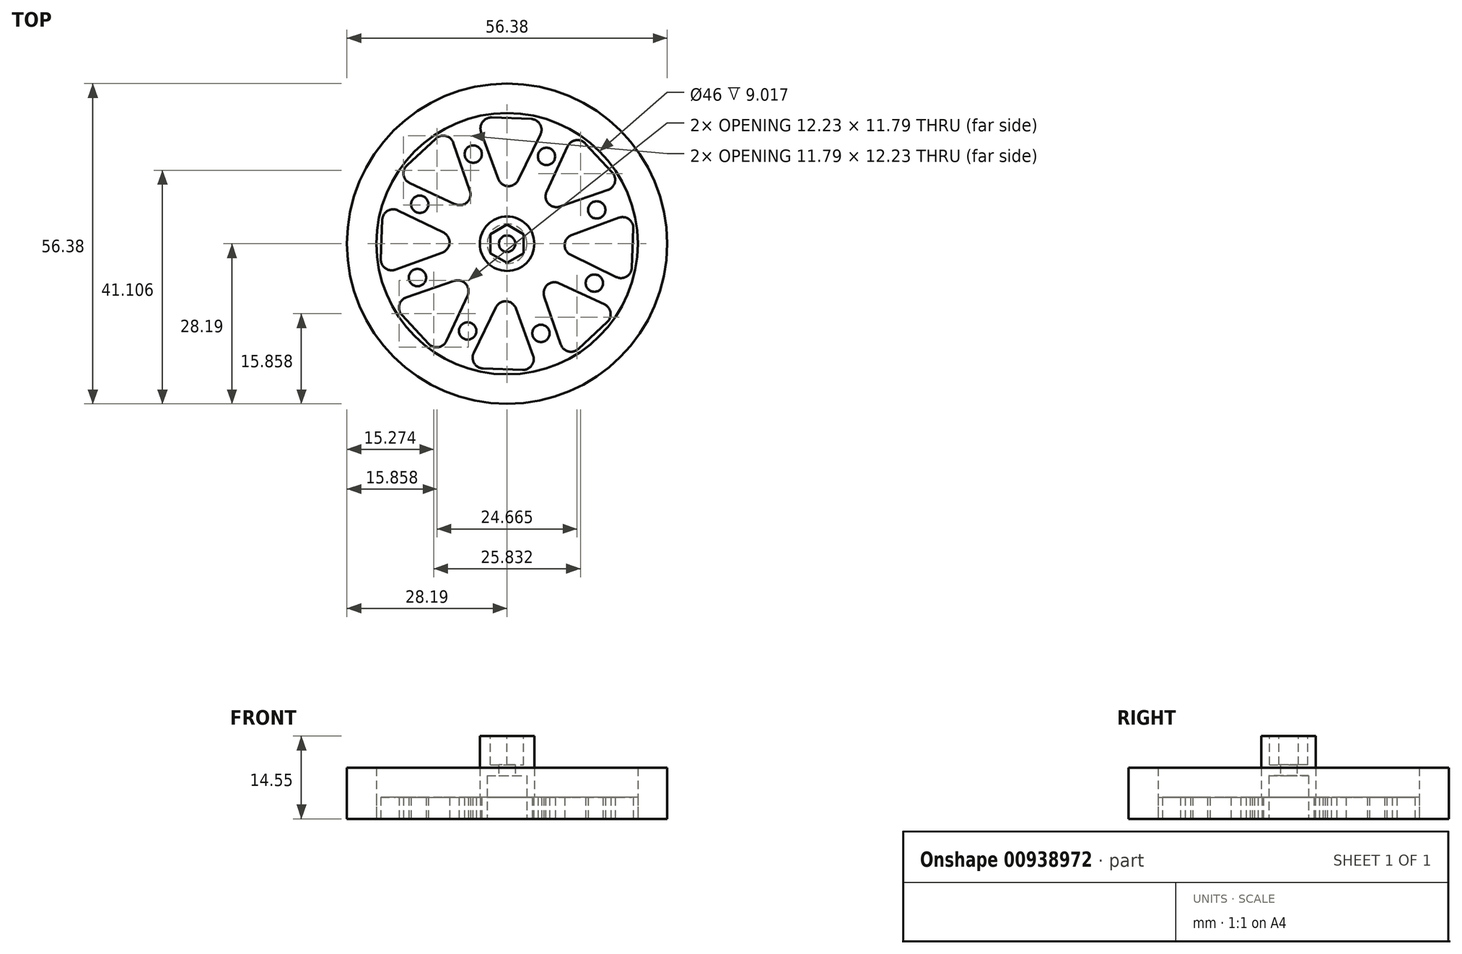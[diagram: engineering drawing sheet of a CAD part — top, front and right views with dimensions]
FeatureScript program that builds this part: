
annotation { "Feature Type Name" : "Feature", "Feature Type Description" : "" }
export const myFeature = defineFeature(function(context is Context, id is Id, definition is map)
    precondition{}
    {
        {
            var Q0;
            Q0=qCreatedBy(makeId("Top.planeOp"),FACE);
            var sketch = newSketch(context, id + "F0", { "sketchPlane" : qUnion([Q0])});
            skCircle(sketch, "E0", {"center": v(0, 0) * mm, "radius": 23 * mm});
            skSolve(sketch);
        }
        {
            var Q0;
            Q0=qSketchRegion(id+"F0",true);
            extrude(context, id + "F1", {"entities" : qUnion([Q0]), "depth" : 3.8 * mm});
        }
        {
            var Q0;
            Q0=makeQuery(id+"F1.opExtrude","CAP_FACE",FACE,{"disambiguationData":[OSD([sQuery(id+"F0.wireOp",EDGE,"E0")])],"isStart":true});
            var sketch = newSketch(context, id + "F2", { "sketchPlane" : qUnion([Q0])});
            skLineSegment(sketch, "E1.0", {"start": v(4.22, -21.97) * mm, "end": v(-2.71, -22.22) * mm});
            skLineSegment(sketch, "E1.1", {"start": v(-4.57, -19.66) * mm, "end": v(-1.54, -11.39) * mm});
            skLineSegment(sketch, "E1.2", {"start": v(1.96, -11.2) * mm, "end": v(5.87, -19.23) * mm});
            skPoint(sketch, "E1.0.midPoint", {"position": v(0.8, -22.1) * mm});
            skLineSegment(sketch, "E2.1.0", {"start": v(10.67, -17.13) * mm, "end": v(6.96, -9.14) * mm});
            skLineSegment(sketch, "E2.1.1", {"start": v(9.31, -6.54) * mm, "end": v(17.75, -9.45) * mm});
            skLineSegment(sketch, "E2.1.2", {"start": v(18.52, -12.55) * mm, "end": v(13.8, -17.63) * mm});
            skLineSegment(sketch, "E2.2.0", {"start": v(19.66, -4.57) * mm, "end": v(11.39, -1.54) * mm});
            skLineSegment(sketch, "E2.2.1", {"start": v(11.2, 1.96) * mm, "end": v(19.23, 5.87) * mm});
            skLineSegment(sketch, "E2.2.2", {"start": v(21.97, 4.22) * mm, "end": v(22.22, -2.71) * mm});
            skLineSegment(sketch, "E2.3.0", {"start": v(17.13, 10.67) * mm, "end": v(9.14, 6.96) * mm});
            skLineSegment(sketch, "E2.3.1", {"start": v(6.54, 9.31) * mm, "end": v(9.45, 17.75) * mm});
            skLineSegment(sketch, "E2.3.2", {"start": v(12.55, 18.52) * mm, "end": v(17.63, 13.8) * mm});
            skLineSegment(sketch, "E2.4.0", {"start": v(4.57, 19.66) * mm, "end": v(1.54, 11.39) * mm});
            skLineSegment(sketch, "E2.4.1", {"start": v(-1.96, 11.2) * mm, "end": v(-5.87, 19.23) * mm});
            skLineSegment(sketch, "E2.4.2", {"start": v(-4.22, 21.97) * mm, "end": v(2.71, 22.22) * mm});
            skLineSegment(sketch, "E2.5.0", {"start": v(-10.67, 17.13) * mm, "end": v(-6.96, 9.14) * mm});
            skLineSegment(sketch, "E2.5.1", {"start": v(-9.31, 6.54) * mm, "end": v(-17.75, 9.45) * mm});
            skLineSegment(sketch, "E2.5.2", {"start": v(-18.52, 12.55) * mm, "end": v(-13.8, 17.63) * mm});
            skLineSegment(sketch, "E2.6.0", {"start": v(-19.66, 4.57) * mm, "end": v(-11.39, 1.54) * mm});
            skLineSegment(sketch, "E2.6.1", {"start": v(-11.2, -1.96) * mm, "end": v(-19.23, -5.87) * mm});
            skLineSegment(sketch, "E2.6.2", {"start": v(-21.97, -4.22) * mm, "end": v(-22.22, 2.71) * mm});
            skLineSegment(sketch, "E2.7.0", {"start": v(-17.13, -10.67) * mm, "end": v(-9.14, -6.96) * mm});
            skLineSegment(sketch, "E2.7.1", {"start": v(-6.54, -9.31) * mm, "end": v(-9.45, -17.75) * mm});
            skLineSegment(sketch, "E2.7.2", {"start": v(-12.55, -18.52) * mm, "end": v(-17.63, -13.8) * mm});
            skPoint(sketch, "E2.center", {"position": v(0, 0) * mm});
            skLineSegment(sketch, "E3", {"start": v(0.8, -22.1) * mm, "end": v(0, -7.18) * mm, "construction": true});
            skLineSegment(sketch, "E4", {"start": v(-11.86, 19.7) * mm, "end": v(-7.15, 21.86) * mm, "construction": true});
            skLineSegment(sketch, "E5", {"start": v(0, 7.18) * mm, "end": v(0, 0) * mm, "construction": true});
            skLineSegment(sketch, "E6", {"start": v(-7.18, 0) * mm, "end": v(7.18, 0) * mm, "construction": true});
            skPoint(sketch, "E7.visualSharp", {"position": v(-19.7, -11.86) * mm});
            skArc(sketch, "E7.filletArc", {"start": v(-17.13, -10.67) * mm, "mid": v(-18.21, -12.1) * mm, "end": v(-17.63, -13.8) * mm});
            skPoint(sketch, "E8.visualSharp", {"position": v(-10.4, -20.51) * mm});
            skArc(sketch, "E8.filletArc", {"start": v(-12.55, -18.52) * mm, "mid": v(-10.79, -18.97) * mm, "end": v(-9.45, -17.75) * mm});
            skPoint(sketch, "E9.visualSharp", {"position": v(-5.08, -5.08) * mm});
            skArc(sketch, "E9.filletArc", {"start": v(-6.54, -9.31) * mm, "mid": v(-7.06, -7.28) * mm, "end": v(-9.14, -6.96) * mm});
            skPoint(sketch, "E10.visualSharp", {"position": v(-7.18, 0) * mm});
            skArc(sketch, "E10.filletArc", {"start": v(-11.2, -1.96) * mm, "mid": v(-10.14, -0.15) * mm, "end": v(-11.39, 1.54) * mm});
            skPoint(sketch, "E11.visualSharp", {"position": v(-22.32, 5.55) * mm});
            skArc(sketch, "E11.filletArc", {"start": v(-19.66, 4.57) * mm, "mid": v(-21.43, 4.32) * mm, "end": v(-22.22, 2.71) * mm});
            skPoint(sketch, "E12.visualSharp", {"position": v(-21.86, -7.15) * mm});
            skArc(sketch, "E12.filletArc", {"start": v(-21.97, -4.22) * mm, "mid": v(-21.04, -5.79) * mm, "end": v(-19.23, -5.87) * mm});
            skPoint(sketch, "E13.visualSharp", {"position": v(-20.51, 10.4) * mm});
            skArc(sketch, "E13.filletArc", {"start": v(-18.52, 12.55) * mm, "mid": v(-18.97, 10.79) * mm, "end": v(-17.75, 9.45) * mm});
            skPoint(sketch, "E14.visualSharp", {"position": v(-11.86, 19.7) * mm});
            skArc(sketch, "E14.filletArc", {"start": v(-10.67, 17.13) * mm, "mid": v(-12.1, 18.21) * mm, "end": v(-13.8, 17.63) * mm});
            skPoint(sketch, "E15.visualSharp", {"position": v(-5.08, 5.08) * mm});
            skArc(sketch, "E15.filletArc", {"start": v(-9.31, 6.54) * mm, "mid": v(-7.28, 7.06) * mm, "end": v(-6.96, 9.14) * mm});
            skPoint(sketch, "E16.visualSharp", {"position": v(0, 7.18) * mm});
            skArc(sketch, "E16.filletArc", {"start": v(-1.96, 11.2) * mm, "mid": v(-0.15, 10.14) * mm, "end": v(1.54, 11.39) * mm});
            skPoint(sketch, "E17.visualSharp", {"position": v(-7.15, 21.86) * mm});
            skArc(sketch, "E17.filletArc", {"start": v(-4.22, 21.97) * mm, "mid": v(-5.79, 21.04) * mm, "end": v(-5.87, 19.23) * mm});
            skPoint(sketch, "E18.visualSharp", {"position": v(5.55, 22.32) * mm});
            skArc(sketch, "E18.filletArc", {"start": v(4.57, 19.66) * mm, "mid": v(4.32, 21.43) * mm, "end": v(2.71, 22.22) * mm});
            skPoint(sketch, "E19.visualSharp", {"position": v(5.08, 5.08) * mm});
            skArc(sketch, "E19.filletArc", {"start": v(6.54, 9.31) * mm, "mid": v(7.06, 7.28) * mm, "end": v(9.14, 6.96) * mm});
            skPoint(sketch, "E20.visualSharp", {"position": v(10.4, 20.51) * mm});
            skArc(sketch, "E20.filletArc", {"start": v(12.55, 18.52) * mm, "mid": v(10.79, 18.97) * mm, "end": v(9.45, 17.75) * mm});
            skPoint(sketch, "E21.visualSharp", {"position": v(19.7, 11.86) * mm});
            skArc(sketch, "E21.filletArc", {"start": v(17.13, 10.67) * mm, "mid": v(18.21, 12.1) * mm, "end": v(17.63, 13.8) * mm});
            skPoint(sketch, "E22.visualSharp", {"position": v(21.86, 7.15) * mm});
            skArc(sketch, "E22.filletArc", {"start": v(21.97, 4.22) * mm, "mid": v(21.04, 5.79) * mm, "end": v(19.23, 5.87) * mm});
            skPoint(sketch, "E23.visualSharp", {"position": v(7.18, 0) * mm});
            skArc(sketch, "E23.filletArc", {"start": v(11.2, 1.96) * mm, "mid": v(10.14, 0.15) * mm, "end": v(11.39, -1.54) * mm});
            skPoint(sketch, "E24.visualSharp", {"position": v(22.32, -5.55) * mm});
            skArc(sketch, "E24.filletArc", {"start": v(19.66, -4.57) * mm, "mid": v(21.43, -4.32) * mm, "end": v(22.22, -2.71) * mm});
            skPoint(sketch, "E25.visualSharp", {"position": v(11.86, -19.7) * mm});
            skArc(sketch, "E25.filletArc", {"start": v(10.67, -17.13) * mm, "mid": v(12.1, -18.21) * mm, "end": v(13.8, -17.63) * mm});
            skPoint(sketch, "E26.visualSharp", {"position": v(5.08, -5.08) * mm});
            skArc(sketch, "E26.filletArc", {"start": v(9.31, -6.54) * mm, "mid": v(7.28, -7.06) * mm, "end": v(6.96, -9.14) * mm});
            skPoint(sketch, "E27.visualSharp", {"position": v(20.51, -10.4) * mm});
            skArc(sketch, "E27.filletArc", {"start": v(18.52, -12.55) * mm, "mid": v(18.97, -10.79) * mm, "end": v(17.75, -9.45) * mm});
            skPoint(sketch, "E28.visualSharp", {"position": v(0, -7.18) * mm});
            skArc(sketch, "E28.filletArc", {"start": v(1.96, -11.2) * mm, "mid": v(0.15, -10.14) * mm, "end": v(-1.54, -11.39) * mm});
            skPoint(sketch, "E29.visualSharp", {"position": v(-5.55, -22.32) * mm});
            skArc(sketch, "E29.filletArc", {"start": v(-4.57, -19.66) * mm, "mid": v(-4.32, -21.43) * mm, "end": v(-2.71, -22.22) * mm});
            skPoint(sketch, "E30.visualSharp", {"position": v(7.15, -21.86) * mm});
            skArc(sketch, "E30.filletArc", {"start": v(4.22, -21.97) * mm, "mid": v(5.79, -21.04) * mm, "end": v(5.87, -19.23) * mm});
            skSolve(sketch);
        }
        {
            var Q0;
            {var subQ11=sQuery(id+"F2.wireOp",EDGE,"E1.1");Q0=makeQuery(id+"F2.imprint","IMPRINT",FACE,{"disambiguationData":[TD([[makeQuery(id+"F2.imprint","IMPRINT",EDGE,{"derivedFrom":subQ11}),1.0]])]});}
            var sketch = newSketch(context, id + "F3", { "sketchPlane" : qUnion([Q0])});
            skCircle(sketch, "E31", {"center": v(0, 0) * mm, "radius": 4.8 * mm});
            skSolve(sketch);
        }
        {
            var Q0;
            Q0=qSketchRegion(id+"F3",true);
            extrude(context, id + "F4", {"entities" : qUnion([Q0]), "operationType" : NewBodyOperationType.ADD, "oppositeDirection" : true, "depth" : 14.55 * mm});
        }
        {
            var Q0;
            Q0=makeQuery(id+"F3.imprint","IMPRINT",FACE,{"disambiguationData":[TD([[makeQuery(id+"F3.imprint","IMPRINT",EDGE,{"derivedFrom":sQuery(id+"F3.wireOp",EDGE,"E31")}),1.0]])]});
            var sketch = newSketch(context, id + "F5", { "sketchPlane" : qUnion([Q0])});
            skCircle(sketch, "E32", {"center": v(0, 0) * mm, "radius": 3.5 * mm});
            skSolve(sketch);
        }
        {
            var Q0;
            Q0=qSketchRegion(id+"F5",true);
            extrude(context, id + "F6", {"entities" : qUnion([Q0]), "operationType" : NewBodyOperationType.REMOVE, "oppositeDirection" : true, "depth" : 7.62 * mm});
        }
        {
            var Q0;
            Q0=makeQuery(id+"F4.opExtrude","CAP_FACE",FACE,{"disambiguationData":[OSD([sQuery(id+"F3.wireOp",EDGE,"E31")])],"isStart":false});
            var sketch = newSketch(context, id + "F7", { "sketchPlane" : qUnion([Q0])});
            skCircle(sketch, "E33.cCircle", {"center": v(0, 0) * mm, "radius": 2.93 * mm, "construction": true});
            skLineSegment(sketch, "E33.0", {"start": v(2.93, 1.69) * mm, "end": v(2.93, -1.69) * mm});
            skLineSegment(sketch, "E33.1", {"start": v(2.93, -1.69) * mm, "end": v(0, -3.38) * mm});
            skLineSegment(sketch, "E33.2", {"start": v(0, -3.38) * mm, "end": v(-2.93, -1.69) * mm});
            skLineSegment(sketch, "E33.3", {"start": v(-2.93, -1.69) * mm, "end": v(-2.93, 1.69) * mm});
            skLineSegment(sketch, "E33.4", {"start": v(-2.93, 1.69) * mm, "end": v(0, 3.38) * mm});
            skLineSegment(sketch, "E33.5", {"start": v(0, 3.38) * mm, "end": v(2.93, 1.69) * mm});
            skPoint(sketch, "E33.0.midPoint", {"position": v(2.93, 0) * mm});
            skSolve(sketch);
        }
        {
            var Q0;
            Q0=makeQuery(id+"F7.imprint","IMPRINT",FACE,{"disambiguationData":[TD([[makeQuery(id+"F7.imprint","IMPRINT",EDGE,{"derivedFrom":sQuery(id+"F7.wireOp",EDGE,"E33.0")}),-1.0]])]});
            extrude(context, id + "F8", {"entities" : qUnion([Q0]), "operationType" : NewBodyOperationType.REMOVE, "oppositeDirection" : true, "depth" : 5.08 * mm});
        }
        {
            var Q0;
            {var subQ11=sQuery(id+"F2.wireOp",EDGE,"E1.1");Q0=makeQuery(id+"F2.imprint","IMPRINT",FACE,{"disambiguationData":[TD([[makeQuery(id+"F2.imprint","IMPRINT",EDGE,{"derivedFrom":subQ11}),1.0]])]});}
            var sketch = newSketch(context, id + "F9", { "sketchPlane" : qUnion([Q0])});
            skCircle(sketch, "E34", {"center": v(0, 0) * mm, "radius": 1.45 * mm});
            skSolve(sketch);
        }
        {
            var Q0;
            Q0=qSketchRegion(id+"F9",true);
            extrude(context, id + "F10", {"entities" : qUnion([Q0]), "operationType" : NewBodyOperationType.REMOVE, "oppositeDirection" : true, "depth" : 25.4 * mm});
        }
        {
            var Q0;
            {var subQ11=sQuery(id+"F2.wireOp",EDGE,"E1.1");Q0=makeQuery(id+"F2.imprint","IMPRINT",FACE,{"disambiguationData":[TD([[makeQuery(id+"F2.imprint","IMPRINT",EDGE,{"derivedFrom":subQ11}),1.0]])]});}
            var sketch = newSketch(context, id + "F11", { "sketchPlane" : qUnion([Q0])});
            skLineSegment(sketch, "E35", {"start": v(8.77, 15.77) * mm, "end": v(3.15, 15.77) * mm, "construction": true});
            skCircle(sketch, "E36", {"center": v(5.96, 15.77) * mm, "radius": 1.52 * mm});
            skCircle(sketch, "E37.1.0", {"center": v(-6.94, 15.37) * mm, "radius": 1.52 * mm});
            skCircle(sketch, "E37.2.0", {"center": v(-15.77, 5.96) * mm, "radius": 1.52 * mm});
            skCircle(sketch, "E37.3.0", {"center": v(-15.37, -6.94) * mm, "radius": 1.52 * mm});
            skCircle(sketch, "E37.4.0", {"center": v(-5.96, -15.77) * mm, "radius": 1.52 * mm});
            skCircle(sketch, "E37.5.0", {"center": v(6.94, -15.37) * mm, "radius": 1.52 * mm});
            skCircle(sketch, "E37.6.0", {"center": v(15.77, -5.96) * mm, "radius": 1.52 * mm});
            skCircle(sketch, "E37.7.0", {"center": v(15.37, 6.94) * mm, "radius": 1.52 * mm});
            skPoint(sketch, "E37.center", {"position": v(0, 0) * mm});
            skSolve(sketch);
        }
        {
            var Q0;
            Q0=qSketchRegion(id+"F11",true);
            extrude(context, id + "F12", {"entities" : qUnion([Q0]), "operationType" : NewBodyOperationType.REMOVE, "oppositeDirection" : true, "depth" : 12.7 * mm});
        }
        {
            var Q0;
            Q0=makeQuery(id+"F3.imprint","IMPRINT",FACE,{"disambiguationData":[TD([[makeQuery(id+"F3.imprint","IMPRINT",EDGE,{"derivedFrom":sQuery(id+"F3.wireOp",EDGE,"E31")}),-1.0]])]});
            var sketch = newSketch(context, id + "F13", { "sketchPlane" : qUnion([Q0])});
            skCircle(sketch, "E38", {"center": v(0, 0) * mm, "radius": 28.2 * mm});
            skCircle(sketch, "E39", {"center": v(0, 0) * mm, "radius": 23 * mm});
            skSolve(sketch);
        }
        {
            var Q0;
            Q0=qSketchRegion(id+"F2",true);
            extrude(context, id + "F14", {"entities" : qUnion([Q0]), "operationType" : NewBodyOperationType.REMOVE, "oppositeDirection" : true, "depth" : 12.7 * mm, "offsetDistance" : 25 * mm});
        }
        {
            var Q0;
            Q0=qSketchRegion(id+"F13",true);
            extrude(context, id + "F15", {"entities" : qUnion([Q0]), "oppositeDirection" : true, "depth" : 9.02 * mm});
        }
    });
